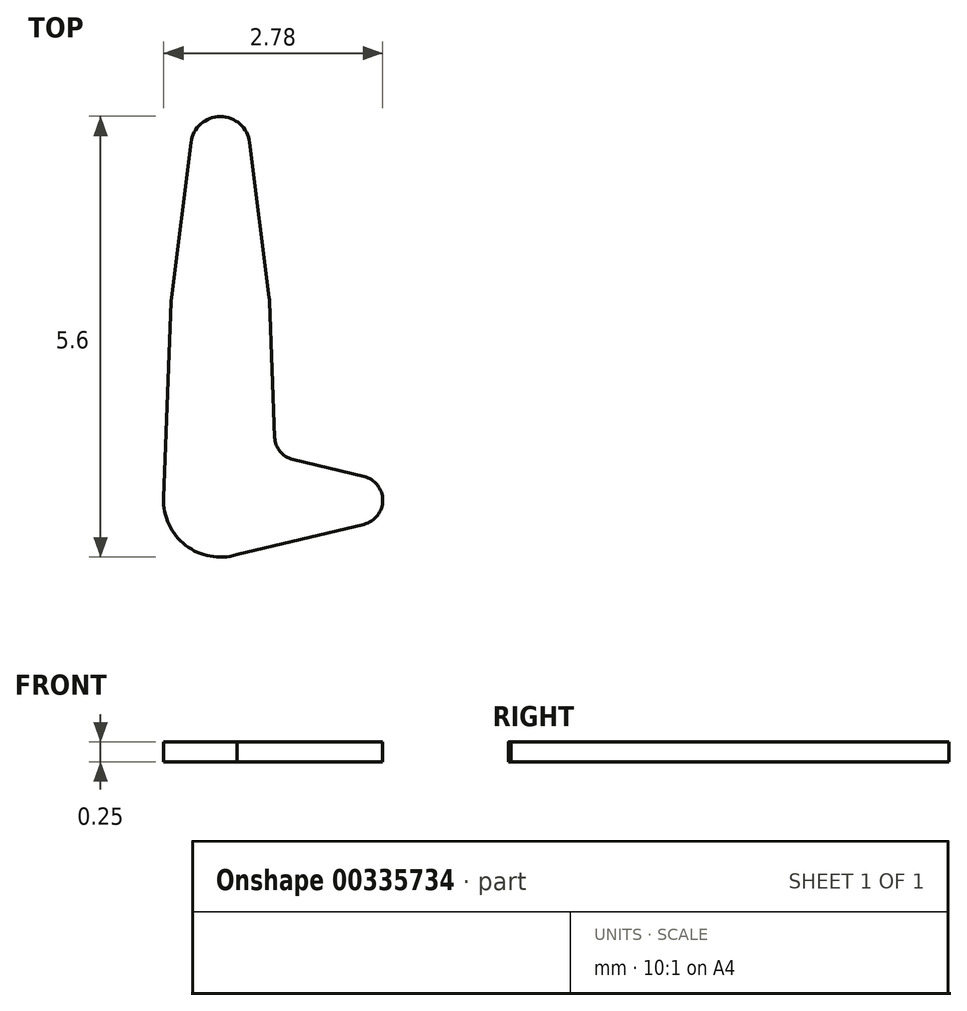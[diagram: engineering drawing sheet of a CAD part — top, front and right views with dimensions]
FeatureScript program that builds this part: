
annotation { "Feature Type Name" : "Feature", "Feature Type Description" : "" }
export const myFeature = defineFeature(function(context is Context, id is Id, definition is map)
    precondition{}
    {
        {
            var Q0;
            Q0=qCreatedBy(makeId("Top.planeOp"),FACE);
            var sketch = newSketch(context, id + "F0", { "sketchPlane" : qUnion([Q0])});
            skLineSegment(sketch, "E0", {"start": v(0, 0) * mm, "end": v(0, 4.5) * mm, "construction": true});
            skCircle(sketch, "E1", {"center": v(0, 0) * mm, "radius": 0.72 * mm});
            skCircle(sketch, "E2", {"center": v(0, 4.5) * mm, "radius": 0.38 * mm});
            skCircle(sketch, "E3", {"center": v(0, 2.5) * mm, "radius": 0.63 * mm});
            skLineSegment(sketch, "E4", {"start": v(0, 0) * mm, "end": v(1.75, 0) * mm, "construction": true});
            skCircle(sketch, "E5", {"center": v(1.75, 0) * mm, "radius": 0.31 * mm});
            skLineSegment(sketch, "E6", {"start": v(-0.37, 4.55) * mm, "end": v(-0.62, 2.58) * mm});
            skLineSegment(sketch, "E7", {"start": v(-0.62, 2.52) * mm, "end": v(-0.72, 0.03) * mm});
            skLineSegment(sketch, "E8", {"start": v(0.37, 4.55) * mm, "end": v(0.62, 2.58) * mm});
            skLineSegment(sketch, "E9", {"start": v(0.62, 2.52) * mm, "end": v(0.7, 0.8) * mm});
            skLineSegment(sketch, "E10", {"start": v(0.92, 0.52) * mm, "end": v(1.82, 0.3) * mm});
            skLineSegment(sketch, "E11", {"start": v(0.21, -0.69) * mm, "end": v(1.82, -0.3) * mm});
            skPoint(sketch, "E12.newPointB", {"position": v(0.21, 0.7) * mm});
            skArc(sketch, "E12.filletArc", {"start": v(0.7, 0.8) * mm, "mid": v(0.76, 0.62) * mm, "end": v(0.92, 0.52) * mm});
            skSolve(sketch);
        }
        {
            var Q0;
            {var subQ0=sQuery(id+"F0.wireOp",EDGE,"E6");Q0=makeQuery(id+"F0.imprint","IMPRINT",FACE,{"disambiguationData":[TD([[makeQuery(id+"F0.imprint","IMPRINT",EDGE,{"derivedFrom":subQ0}),1.0]])]});}
            var Q1;
            {var subQ3=sQuery(id+"F0.wireOp",EDGE,"E7");Q1=makeQuery(id+"F0.imprint","IMPRINT",FACE,{"disambiguationData":[TD([[makeQuery(id+"F0.imprint","IMPRINT",EDGE,{"derivedFrom":subQ3}),1.0]])]});}
            var Q2;
            {var subQ0=sQuery(id+"F0.wireOp",EDGE,"E1");var subQ1=makeQuery(id+"F0.imprint","INTERSECT",VERTEX,{"derivedFrom":[subQ0,sQuery(id+"F0.wireOp",EDGE,"E7")]});Q2=makeQuery(id+"F0.imprint","IMPRINT",FACE,{"disambiguationData":[TD([[makeQuery(id+"F0.imprint","IMPRINT",EDGE,{"disambiguationData":[TD([[subQ1,-1.0]])],"derivedFrom":subQ0}),1.0]])]});}
            var Q3;
            {var subQ0=sQuery(id+"F0.wireOp",EDGE,"E2");var subQ1=makeQuery(id+"F0.imprint","INTERSECT",VERTEX,{"derivedFrom":[subQ0,sQuery(id+"F0.wireOp",EDGE,"E6")]});Q3=makeQuery(id+"F0.imprint","IMPRINT",FACE,{"disambiguationData":[TD([[makeQuery(id+"F0.imprint","IMPRINT",EDGE,{"disambiguationData":[TD([[subQ1,1.0]])],"derivedFrom":subQ0}),1.0]])]});}
            var Q4;
            {var subQ0=sQuery(id+"F0.wireOp",EDGE,"E3");var subQ1=makeQuery(id+"F0.imprint","INTERSECT",VERTEX,{"derivedFrom":[subQ0,sQuery(id+"F0.wireOp",EDGE,"E8")]});Q4=makeQuery(id+"F0.imprint","IMPRINT",FACE,{"disambiguationData":[TD([[makeQuery(id+"F0.imprint","IMPRINT",EDGE,{"disambiguationData":[TD([[subQ1,1.0]])],"derivedFrom":subQ0}),1.0]])]});}
            var Q5;
            {var subQ0=sQuery(id+"F0.wireOp",EDGE,"E5");var subQ1=makeQuery(id+"F0.imprint","INTERSECT",VERTEX,{"derivedFrom":[subQ0,sQuery(id+"F0.wireOp",EDGE,"E10")]});Q5=makeQuery(id+"F0.imprint","IMPRINT",FACE,{"disambiguationData":[TD([[makeQuery(id+"F0.imprint","IMPRINT",EDGE,{"disambiguationData":[TD([[subQ1,-1.0]])],"derivedFrom":subQ0}),1.0]])]});}
            extrude(context, id + "F1", {"entities" : qUnion([Q0, Q1, Q2, Q3, Q4, Q5]), "depth" : 0.25 * mm});
        }
    });
